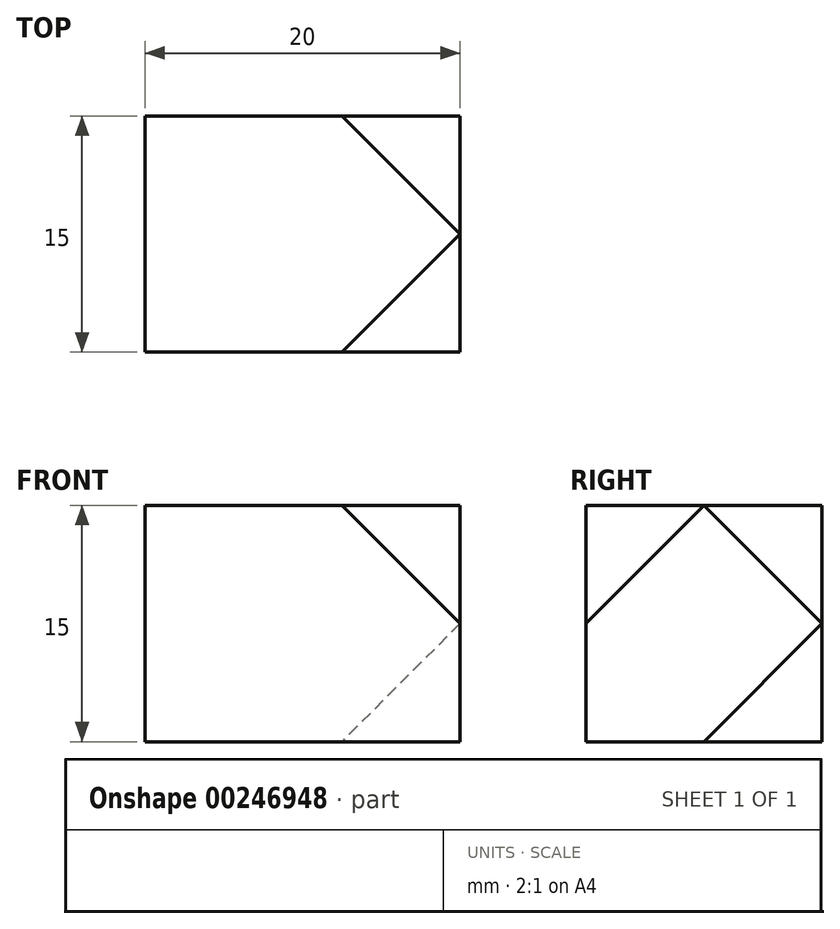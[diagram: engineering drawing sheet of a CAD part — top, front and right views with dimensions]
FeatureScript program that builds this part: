
annotation { "Feature Type Name" : "Feature", "Feature Type Description" : "" }
export const myFeature = defineFeature(function(context is Context, id is Id, definition is map)
    precondition{}
    {
        {
            var Q0;
            Q0=qCreatedBy(makeId("Front.planeOp"),FACE);
            var sketch = newSketch(context, id + "F0", { "sketchPlane" : qUnion([Q0])});
            skLineSegment(sketch, "E0", {"start": v(0, 15) * mm, "end": v(0, 0) * mm});
            skLineSegment(sketch, "E1", {"start": v(20, 15) * mm, "end": v(20, 7.5) * mm});
            skLineSegment(sketch, "E2", {"start": v(20, 7.5) * mm, "end": v(20, 0) * mm});
            skLineSegment(sketch, "E3", {"start": v(12.5, 0) * mm, "end": v(20, 0) * mm});
            skLineSegment(sketch, "E4", {"start": v(20, 7.5) * mm, "end": v(12.5, 0) * mm});
            skLineSegment(sketch, "E5", {"start": v(20, 7.5) * mm, "end": v(12.5, 15) * mm});
            skLineSegment(sketch, "E6", {"start": v(0, 15) * mm, "end": v(12.5, 15) * mm});
            skLineSegment(sketch, "E7", {"start": v(20, 15) * mm, "end": v(12.5, 15) * mm});
            skLineSegment(sketch, "E8", {"start": v(0, 0) * mm, "end": v(12.5, 0) * mm});
            skLineSegment(sketch, "E9", {"start": v(12.5, 15) * mm, "end": v(12.5, 0) * mm});
            skSolve(sketch);
        }
        {
            var Q0;
            Q0=makeQuery(id+"F0.imprint","IMPRINT",FACE,{"disambiguationData":[TD([[makeQuery(id+"F0.imprint","IMPRINT",EDGE,{"derivedFrom":sQuery(id+"F0.wireOp",EDGE,"E0")}),1.0]])]});
            var Q1;
            Q1=makeQuery(id+"F0.imprint","IMPRINT",FACE,{"disambiguationData":[TD([[makeQuery(id+"F0.imprint","IMPRINT",EDGE,{"derivedFrom":sQuery(id+"F0.wireOp",EDGE,"E1")}),-1.0]])]});
            var Q2;
            Q2=makeQuery(id+"F0.imprint","IMPRINT",FACE,{"disambiguationData":[TD([[makeQuery(id+"F0.imprint","IMPRINT",EDGE,{"derivedFrom":sQuery(id+"F0.wireOp",EDGE,"E2")}),-1.0]])]});
            var Q3;
            Q3=makeQuery(id+"F0.imprint","IMPRINT",FACE,{"disambiguationData":[TD([[makeQuery(id+"F0.imprint","IMPRINT",EDGE,{"derivedFrom":sQuery(id+"F0.wireOp",EDGE,"E4")}),-1.0]])]});
            extrude(context, id + "F1", {"entities" : qUnion([Q0, Q1, Q2, Q3]), "depth" : 15 * mm});
        }
        {
            var Q0;
            Q0=qCreatedBy(makeId("Top.planeOp"),FACE);
            var sketch = newSketch(context, id + "F2", { "sketchPlane" : qUnion([Q0])});
            skLineSegment(sketch, "E10", {"start": v(0, 0) * mm, "end": v(20, 0) * mm});
            skLineSegment(sketch, "E11", {"start": v(20, -15) * mm, "end": v(0, -15) * mm});
            skLineSegment(sketch, "E12", {"start": v(0, -15) * mm, "end": v(0, 0) * mm});
            skLineSegment(sketch, "E13", {"start": v(20, 0) * mm, "end": v(12.5, 0) * mm});
            skLineSegment(sketch, "E14", {"start": v(12.5, 0) * mm, "end": v(12.5, -15) * mm});
            skLineSegment(sketch, "E15", {"start": v(12.5, -15) * mm, "end": v(20, -7.5) * mm});
            skLineSegment(sketch, "E16", {"start": v(20, -7.5) * mm, "end": v(12.5, 0) * mm});
            skLineSegment(sketch, "E17", {"start": v(20, 0) * mm, "end": v(20, -7.5) * mm});
            skLineSegment(sketch, "E18", {"start": v(20, -15) * mm, "end": v(20, -7.5) * mm});
            skSolve(sketch);
        }
        {
            var Q0;
            Q0=makeQuery(id+"F1.opExtrude","SWEPT_FACE",FACE,{"disambiguationData":[OSD([sQuery(id+"F0.wireOp",EDGE,"E1"),sQuery(id+"F0.wireOp",EDGE,"E2")])]});
            var sketch = newSketch(context, id + "F3", { "sketchPlane" : qUnion([Q0])});
            skLineSegment(sketch, "E19", {"start": v(0, 7.5) * mm, "end": v(-7.5, 0) * mm});
            skLineSegment(sketch, "E20", {"start": v(-7.5, 15) * mm, "end": v(0, 7.5) * mm});
            skLineSegment(sketch, "E21", {"start": v(-15, 7.5) * mm, "end": v(-7.5, 0) * mm});
            skLineSegment(sketch, "E22", {"start": v(-7.5, 15) * mm, "end": v(-15, 7.5) * mm});
            skSolve(sketch);
        }
        {
            var Q0;
            Q0=sQuery(id+"F3.wireOp",VERTEX,"E20.end");
            var Q1;
            Q1=sQuery(id+"F0.wireOp",VERTEX,"E5.end");
            var Q2;
            Q2=sQuery(id+"F3.wireOp",VERTEX,"E20.start");
            cPlane(context, id + "F4", {"entities" : qUnion([Q0, Q1, Q2]), "cplaneType" : CPlaneType.THREE_POINT, "offset" : 25 * mm, "width" : 150 * mm, "height" : 150 * mm});
        }
        {
            var Q0;
            Q0=makeQuery(id+"F1.opExtrude","SWEPT_FACE",FACE,{"disambiguationData":[OSD([sQuery(id+"F0.wireOp",EDGE,"E6"),sQuery(id+"F0.wireOp",EDGE,"E7")])]});
            var sketch = newSketch(context, id + "F5", { "sketchPlane" : qUnion([Q0])});
            skLineSegment(sketch, "E23", {"start": v(20, -7.5) * mm, "end": v(12.5, 0) * mm});
            skLineSegment(sketch, "E24", {"start": v(12.5, 0) * mm, "end": v(12.5, -15) * mm});
            skLineSegment(sketch, "E25", {"start": v(12.5, -15) * mm, "end": v(20, -7.5) * mm});
            skSolve(sketch);
        }
        {
            var Q0;
            Q0=qCreatedBy(id+"F4.planeOp",FACE);
            var sketch = newSketch(context, id + "F6", { "sketchPlane" : qUnion([Q0])});
            skLineSegment(sketch, "E26", {"start": v(13.27, 5.3) * mm, "end": v(4.08, 10.6) * mm});
            skLineSegment(sketch, "E27", {"start": v(4.08, 10.6) * mm, "end": v(13.27, 15.9) * mm});
            skLineSegment(sketch, "E28", {"start": v(13.27, 15.9) * mm, "end": v(13.27, 5.3) * mm});
            skSolve(sketch);
        }
        {
            var Q0;
            Q0 = qSketchRegion(id + "F6", true);
            extrude(context, id + "F7", {"entities" : qUnion([Q0]), "operationType" : NewBodyOperationType.REMOVE, "oppositeDirection" : true, "depth" : 25 * mm});
        }
        {
            var Q0;
            Q0=sQuery(id+"F3.wireOp",VERTEX,"E19.end");
            var Q1;
            Q1=sQuery(id+"F3.wireOp",VERTEX,"E20.end");
            var Q2;
            Q2=sQuery(id+"F0.wireOp",VERTEX,"E4.end");
            cPlane(context, id + "F8", {"entities" : qUnion([Q0, Q1, Q2]), "cplaneType" : CPlaneType.THREE_POINT, "offset" : 25 * mm, "width" : 150 * mm, "height" : 150 * mm});
        }
        {
            var Q0;
            Q0=qCreatedBy(id+"F8.planeOp",FACE);
            var sketch = newSketch(context, id + "F9", { "sketchPlane" : qUnion([Q0])});
            skLineSegment(sketch, "E29", {"start": v(-19.4, -5.3) * mm, "end": v(-19.4, 5.3) * mm});
            skLineSegment(sketch, "E30", {"start": v(-19.4, 5.3) * mm, "end": v(-10.2, 0) * mm});
            skLineSegment(sketch, "E31", {"start": v(-10.2, 0) * mm, "end": v(-19.4, -5.3) * mm});
            skSolve(sketch);
        }
        {
            var Q0;
            Q0 = qSketchRegion(id + "F9", true);
            extrude(context, id + "F10", {"entities" : qUnion([Q0]), "operationType" : NewBodyOperationType.REMOVE, "depth" : 43.5 * mm});
        }
        {
            var Q0;
            Q0=makeQuery(id+"F1.opExtrude","CAP_FACE",FACE,{"disambiguationData":[OSD([sQuery(id+"F0.wireOp",EDGE,"E0"),sQuery(id+"F0.wireOp",EDGE,"E1"),sQuery(id+"F0.wireOp",EDGE,"E2"),sQuery(id+"F0.wireOp",EDGE,"E3"),sQuery(id+"F0.wireOp",EDGE,"E6"),sQuery(id+"F0.wireOp",EDGE,"E7"),sQuery(id+"F0.wireOp",EDGE,"E8")])],"isStart":false});
            var sketch = newSketch(context, id + "F11", { "sketchPlane" : qUnion([Q0])});
            skLineSegment(sketch, "E32", {"start": v(12.5, 0) * mm, "end": v(20, 7.5) * mm});
            skLineSegment(sketch, "E33", {"start": v(20, 7.5) * mm, "end": v(12.5, 15) * mm});
            skSolve(sketch);
        }
        {
            var Q0;
            Q0=sQuery(id+"F3.wireOp",VERTEX,"E21.start");
            var Q1;
            Q1=sQuery(id+"F11.wireOp",VERTEX,"E32.start");
            var Q2;
            Q2=sQuery(id+"F3.wireOp",VERTEX,"E21.end");
            cPlane(context, id + "F12", {"entities" : qUnion([Q0, Q1, Q2]), "cplaneType" : CPlaneType.THREE_POINT, "offset" : 25 * mm, "width" : 150 * mm, "height" : 150 * mm});
        }
        {
            var Q0;
            Q0=qCreatedBy(id+"F12.planeOp",FACE);
            var sketch = newSketch(context, id + "F13", { "sketchPlane" : qUnion([Q0])});
            skLineSegment(sketch, "E34", {"start": v(7.14, 8.84) * mm, "end": v(7.14, 19.45) * mm});
            skLineSegment(sketch, "E35", {"start": v(7.14, 19.45) * mm, "end": v(-2.04, 14.14) * mm});
            skLineSegment(sketch, "E36", {"start": v(-2.04, 14.14) * mm, "end": v(7.14, 8.84) * mm});
            skSolve(sketch);
        }
        {
            var Q0;
            Q0 = qSketchRegion(id + "F13", true);
            extrude(context, id + "F14", {"entities" : qUnion([Q0]), "operationType" : NewBodyOperationType.REMOVE, "oppositeDirection" : true, "depth" : 25 * mm});
        }
        {
            var Q0;
            Q0=sQuery(id+"F11.wireOp",VERTEX,"E33.end");
            var Q1;
            Q1=sQuery(id+"F11.wireOp",VERTEX,"E33.start");
            var Q2;
            Q2=sQuery(id+"F5.wireOp",VERTEX,"E25.end");
            cPlane(context, id + "F15", {"entities" : qUnion([Q0, Q1, Q2]), "cplaneType" : CPlaneType.THREE_POINT, "offset" : 25 * mm, "width" : 150 * mm, "height" : 150 * mm});
        }
        {
            var Q0;
            Q0=qCreatedBy(id+"F15.planeOp",FACE);
            var sketch = newSketch(context, id + "F16", { "sketchPlane" : qUnion([Q0])});
            skLineSegment(sketch, "E37", {"start": v(-7.14, 5.3) * mm, "end": v(-7.14, -5.3) * mm});
            skLineSegment(sketch, "E38", {"start": v(-7.14, 5.3) * mm, "end": v(2.04, 0) * mm});
            skLineSegment(sketch, "E39", {"start": v(2.04, 0) * mm, "end": v(-7.14, -5.3) * mm});
            skSolve(sketch);
        }
        {
            var Q0;
            Q0 = qSketchRegion(id + "F16", true);
            extrude(context, id + "F17", {"entities" : qUnion([Q0]), "operationType" : NewBodyOperationType.REMOVE, "oppositeDirection" : true, "depth" : 25 * mm});
        }
    });
